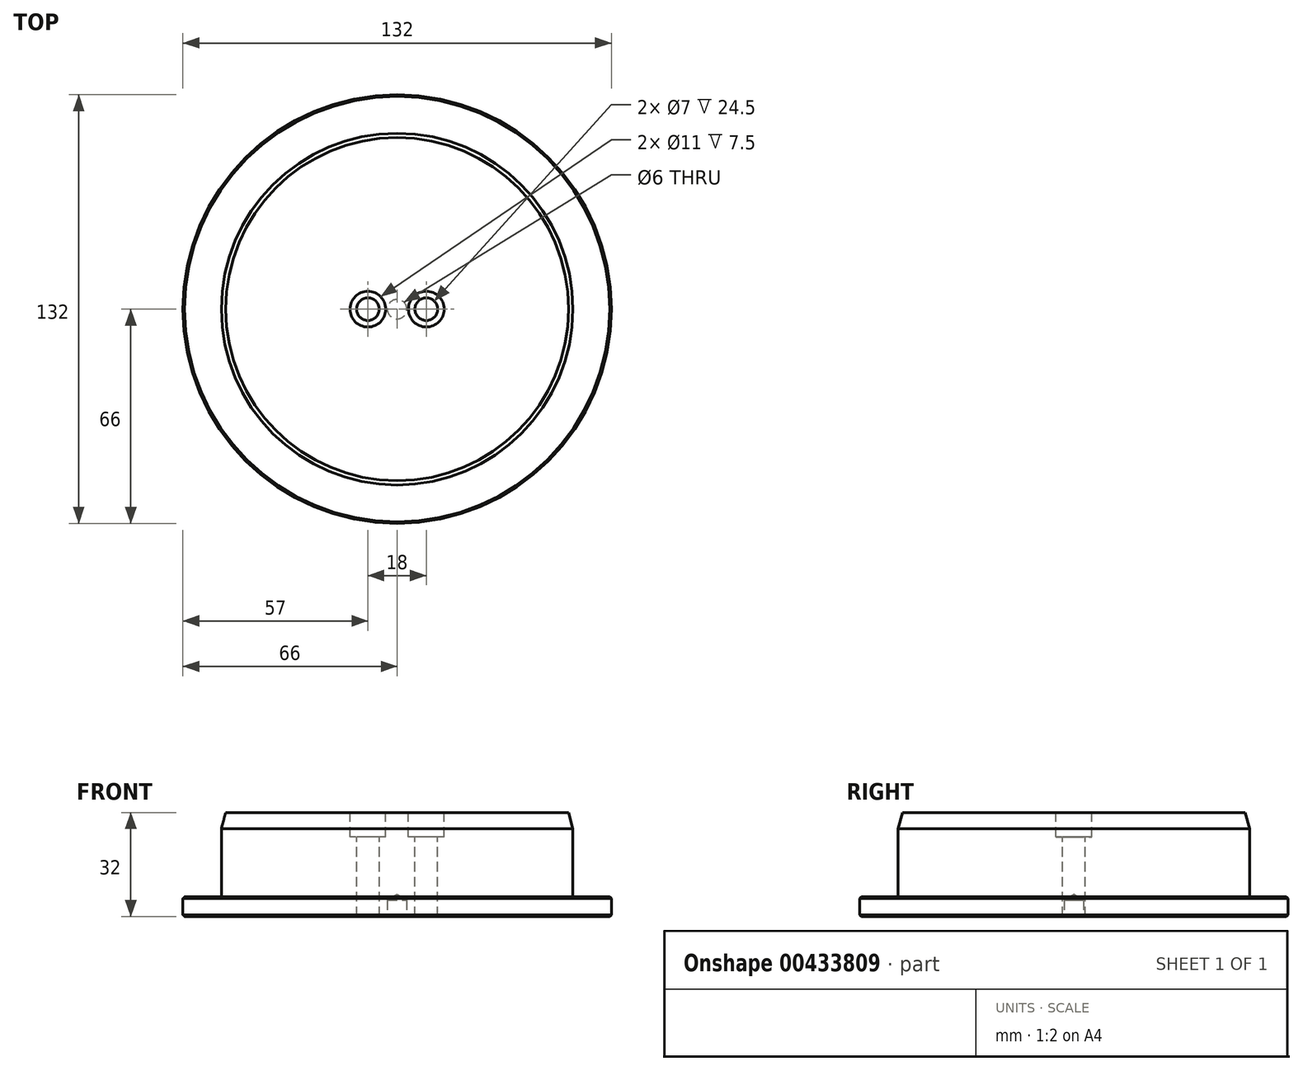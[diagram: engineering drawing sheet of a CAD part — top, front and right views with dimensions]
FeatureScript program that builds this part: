
annotation { "Feature Type Name" : "Feature", "Feature Type Description" : "" }
export const myFeature = defineFeature(function(context is Context, id is Id, definition is map)
    precondition{}
    {
        {
            var Q0;
            Q0=qCreatedBy(makeId("Front.planeOp"),FACE);
            var sketch = newSketch(context, id + "F0", { "sketchPlane" : qUnion([Q0])});
            skLineSegment(sketch, "E0", {"start": v(0, 0) * mm, "end": v(66, 0) * mm});
            skLineSegment(sketch, "E1", {"start": v(0, 0) * mm, "end": v(0, 32) * mm});
            skLineSegment(sketch, "E2.0", {"start": v(66, 0) * mm, "end": v(66, 6) * mm});
            skLineSegment(sketch, "E3.0", {"start": v(0, 32) * mm, "end": v(54.15, 32) * mm});
            skLineSegment(sketch, "E4.0", {"start": v(54.15, 6) * mm, "end": v(54.15, 32) * mm});
            skLineSegment(sketch, "E5.0", {"start": v(54.15, 6) * mm, "end": v(66, 6) * mm});
            skLineSegment(sketch, "E6", {"start": v(0, 0) * mm, "end": v(0, 63.65) * mm});
            skSolve(sketch);
        }
        {
            var Q0;
            {var subQ1=sQuery(id+"F0.wireOp",EDGE,"E0");Q0=makeQuery(id+"F0.imprint","IMPRINT",FACE,{"disambiguationData":[TD([[makeQuery(id+"F0.imprint","IMPRINT",EDGE,{"derivedFrom":subQ1}),1.0]])]});}
            var Q1;
            Q1=sQuery(id+"F0.wireOp",EDGE,"E6");
            revolve(context, id + "F1", {"entities" : qUnion([Q0]), "axis" : qUnion([Q1]), "revolveType" : RevolveType.FULL});
        }
        {
            var Q0;
            Q0=makeQuery(id+"F1.opRevolve","SWEPT_EDGE",EDGE,{"disambiguationData":[OSD([sQuery(id+"F0.wireOp",EDGE,"E2.0"),sQuery(id+"F0.wireOp",EDGE,"E5.0")])]});
            chamfer(context, id + "F2", {"entities" : qUnion([Q0]), "width" : 0.5 * mm, "tangentPropagation" : true});
        }
        {
            var Q0;
            Q0=makeQuery(id+"F1.opRevolve","SWEPT_EDGE",EDGE,{"disambiguationData":[OSD([sQuery(id+"F0.wireOp",EDGE,"E0"),sQuery(id+"F0.wireOp",EDGE,"E2.0")])]});
            chamfer(context, id + "F3", {"entities" : qUnion([Q0]), "width" : 0.5 * mm, "tangentPropagation" : true});
        }
        {
            var Q0;
            Q0=makeQuery(id+"F1.opRevolve","SWEPT_EDGE",EDGE,{"disambiguationData":[OSD([sQuery(id+"F0.wireOp",EDGE,"E3.0"),sQuery(id+"F0.wireOp",EDGE,"E4.0")])]});
            chamfer(context, id + "F4", {"entities" : qUnion([Q0]), "chamferType" : ChamferType.OFFSET_ANGLE, "width" : 5 * mm, "oppositeDirection" : false, "angle" : 15 * degree, "tangentPropagation" : true});
        }
        {
            var Q0;
            Q0=makeQuery(id+"F1.opRevolve","SWEPT_FACE",FACE,{"disambiguationData":[OSD([sQuery(id+"F0.wireOp",EDGE,"E3.0")])]});
            var sketch = newSketch(context, id + "F5", { "sketchPlane" : qUnion([Q0])});
            skCircle(sketch, "E7.0", {"center": v(0, 0) * mm, "radius": 57.81 * mm});
            skCircle(sketch, "E8", {"center": v(9, 0) * mm, "radius": 5.5 * mm});
            skCircle(sketch, "E9", {"center": v(9, 0) * mm, "radius": 3.5 * mm});
            skCircle(sketch, "E10.MirrorC", {"center": v(-9, 0) * mm, "radius": 3.5 * mm});
            skCircle(sketch, "E11.MirrorC", {"center": v(-9, 0) * mm, "radius": 5.5 * mm});
            skSolve(sketch);
        }
        {
            var Q0;
            Q0=sQuery(id+"F5.wireOp",VERTEX,"E10.MirrorC.center");
            var Q1;
            Q1=sQuery(id+"F5.wireOp",VERTEX,"E8.center");
            var Q2;
            Q2=makeQuery(id+"F1.opRevolve","SWEPT_BODY",BODY,{"disambiguationData":[OSD([sQuery(id+"F0.wireOp",EDGE,"E0"),sQuery(id+"F0.wireOp",EDGE,"E2.0"),sQuery(id+"F0.wireOp",EDGE,"E3.0"),sQuery(id+"F0.wireOp",EDGE,"E4.0"),sQuery(id+"F0.wireOp",EDGE,"E5.0"),sQuery(id+"F0.wireOp",EDGE,"E6")])]});
            hole(context, id + "F6", {"style" : HoleStyle.SIMPLE, "endStyle" : HoleEndStyle.THROUGH, "holeDiameter" : 7 * mm, "isTappedThrough" : true, "tappedDepth" : 12 * mm, "tapClearance" : 3, "locations" : qUnion([Q0, Q1]), "scope" : qUnion([Q2])});
        }
        {
            var Q0;
            Q0=sQuery(id+"F5.wireOp",VERTEX,"E8.center");
            var Q1;
            Q1=sQuery(id+"F5.wireOp",VERTEX,"E10.MirrorC.center");
            var Q2;
            Q2=makeQuery(id+"F1.opRevolve","SWEPT_BODY",BODY,{"disambiguationData":[OSD([sQuery(id+"F0.wireOp",EDGE,"E0"),sQuery(id+"F0.wireOp",EDGE,"E2.0"),sQuery(id+"F0.wireOp",EDGE,"E3.0"),sQuery(id+"F0.wireOp",EDGE,"E4.0"),sQuery(id+"F0.wireOp",EDGE,"E5.0"),sQuery(id+"F0.wireOp",EDGE,"E6")])]});
            hole(context, id + "F7", {"style" : HoleStyle.C_BORE, "endStyle" : HoleEndStyle.THROUGH, "holeDiameter" : 7 * mm, "cBoreDiameter" : 11 * mm, "cBoreDepth" : 7.5 * mm, "isTappedThrough" : true, "tappedDepth" : 12 * mm, "tapClearance" : 3, "locations" : qUnion([Q0, Q1]), "scope" : qUnion([Q2])});
        }
        {
            var Q0;
            Q0=makeQuery(id+"F1.opRevolve","SWEPT_FACE",FACE,{"disambiguationData":[OSD([sQuery(id+"F0.wireOp",EDGE,"E0")])]});
            var sketch = newSketch(context, id + "F8", { "sketchPlane" : qUnion([Q0])});
            skPoint(sketch, "E12", {"position": v(0, 0) * mm});
            skSolve(sketch);
        }
        {
            var Q0;
            Q0=sQuery(id+"F8.wireOp",VERTEX,"E12");
            var Q1;
            Q1=makeQuery(id+"F1.opRevolve","SWEPT_BODY",BODY,{"disambiguationData":[OSD([sQuery(id+"F0.wireOp",EDGE,"E0"),sQuery(id+"F0.wireOp",EDGE,"E2.0"),sQuery(id+"F0.wireOp",EDGE,"E3.0"),sQuery(id+"F0.wireOp",EDGE,"E4.0"),sQuery(id+"F0.wireOp",EDGE,"E5.0"),sQuery(id+"F0.wireOp",EDGE,"E6")])]});
            hole(context, id + "F9", {"style" : HoleStyle.SIMPLE, "endStyle" : HoleEndStyle.BLIND, "holeDiameter" : 6 * mm, "holeDepth" : 5 * mm, "isTappedThrough" : true, "tappedDepth" : 12 * mm, "tapClearance" : 3, "locations" : qUnion([Q0]), "scope" : qUnion([Q1])});
        }
    });
